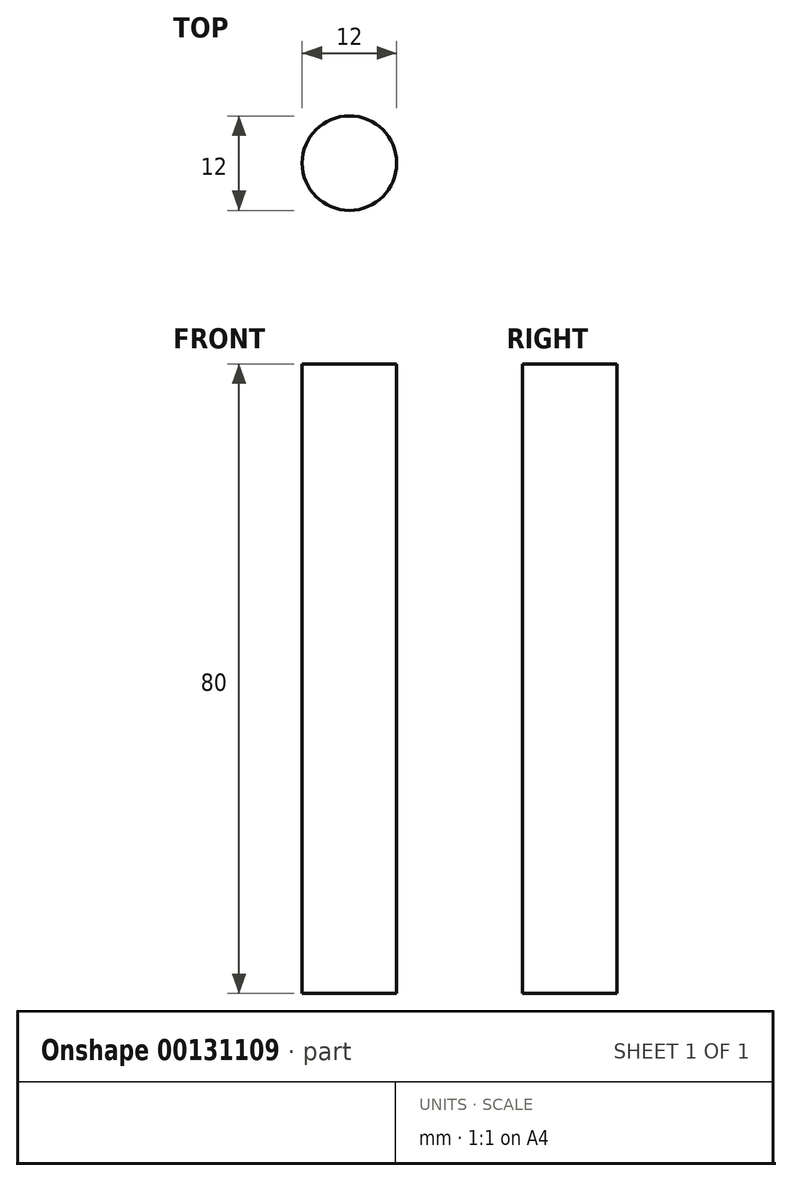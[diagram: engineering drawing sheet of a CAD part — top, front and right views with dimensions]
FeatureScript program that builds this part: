
annotation { "Feature Type Name" : "Feature", "Feature Type Description" : "" }
export const myFeature = defineFeature(function(context is Context, id is Id, definition is map)
    precondition{}
    {
        {
            var Q0;
            Q0=qCreatedBy(makeId("Top.planeOp"),FACE);
            var sketch = newSketch(context, id + "F0", { "sketchPlane" : qUnion([Q0])});
            skCircle(sketch, "E0", {"center": v(0, 0) * mm, "radius": 6 * mm});
            skSolve(sketch);
        }
        {
            var Q0;
            Q0=makeQuery(id+"F0.imprint","IMPRINT",FACE,{"disambiguationData":[TD([[makeQuery(id+"F0.imprint","IMPRINT",EDGE,{"derivedFrom":sQuery(id+"F0.wireOp",EDGE,"E0")}),1.0]])]});
            extrude(context, id + "F1", {"entities" : qUnion([Q0]), "depth" : 80 * mm});
        }
    });
